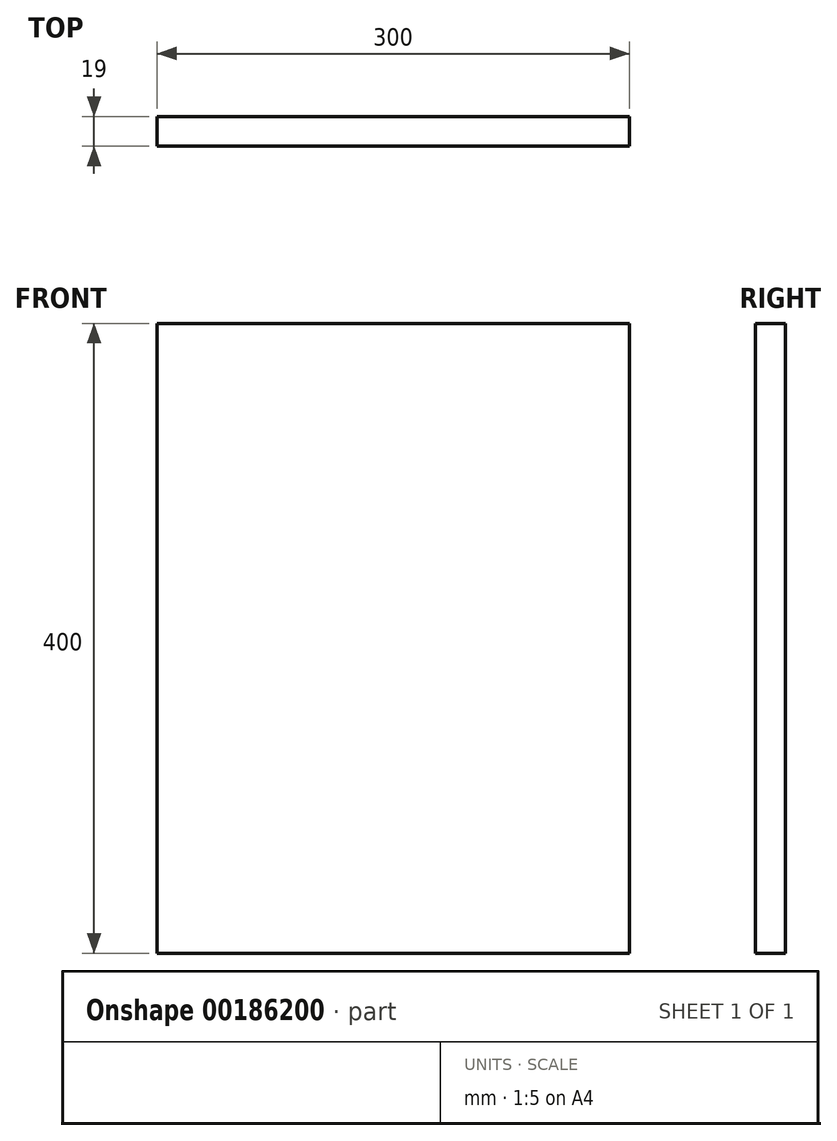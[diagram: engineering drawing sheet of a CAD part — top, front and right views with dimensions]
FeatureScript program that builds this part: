
annotation { "Feature Type Name" : "Feature", "Feature Type Description" : "" }
export const myFeature = defineFeature(function(context is Context, id is Id, definition is map)
    precondition{}
    {
        {
            var Q0;
            Q0=qCreatedBy(makeId("Front.planeOp"),FACE);
            var sketch = newSketch(context, id + "F0", { "sketchPlane" : qUnion([Q0])});
            skLineSegment(sketch, "E0.bottom", {"start": v(-150.15, 224.73) * mm, "end": v(149.85, 224.73) * mm});
            skLineSegment(sketch, "E0.top", {"start": v(-150.15, -175.27) * mm, "end": v(149.85, -175.27) * mm});
            skLineSegment(sketch, "E0.left", {"start": v(-150.15, 224.73) * mm, "end": v(-150.15, -175.27) * mm});
            skLineSegment(sketch, "E0.right", {"start": v(149.85, 224.73) * mm, "end": v(149.85, -175.27) * mm});
            skSolve(sketch);
        }
        {
            var Q0;
            Q0 = qSketchRegion(id + "F0", true);
            extrude(context, id + "F1", {"entities" : qUnion([Q0]), "depth" : 19 * mm});
        }
    });
